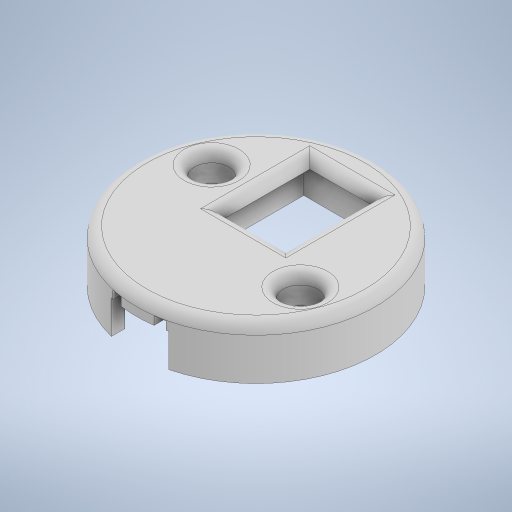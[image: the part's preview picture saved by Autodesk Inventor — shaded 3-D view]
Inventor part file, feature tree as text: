
AUTODESK INVENTOR PART (.ipt)
format: ipt  version: 2023 (Build 270158000, 158)  size: 401,408 bytes
history: native  units: mm
features: extrude x11, sketch x8, fillet x3, plane x2, thread x2, projected_geometry x1
ambient origin geometry x8: Origin, YZ Plane, XZ Plane, XY Plane, X Axis, Y Axis, Z Axis, Center Point
bodies: Solid1 (feature_tree)
feature tree (27):
  sketch  "Sketch1"  dims[d0=30.0mm d1=15.0mm]
  extrude  "Extrusion1"  Depth=30.0mm
  extrude  "Extrusion2"  Depth=16.0mm
  extrude  "Extrusion4"  Depth=8.25mm TaperAngle=0.0deg
  extrude  "Extrusion5"  Depth=8.4mm
  extrude  "Extrusion6"  Depth=1.94mm TaperAngle=0.0deg
  extrude  "Extrusion7"  Depth=1.25mm TaperAngle=0.0deg
  plane  "Work Plane1"
  extrude  "Extrusion9"  Depth=0.3mm
  plane  "Work Plane2"
  fillet  "Fillet3"  Radius=1.5mm
  fillet  "Fillet4"  Radius=1.5mm
  extrude  "Extrusion10"  Depth=1.5mm
  sketch  "Sketch7"  dims[d22=0.3mm d23=0.3mm d24=1.5mm d25=1.5mm]
  extrude  "Extrusion11"  Depth=1.5mm
  extrude  "Extrusion12"  TaperAngle=0.0deg  [1 undecoded]
  fillet  "Fillet5"  [1 undecoded]
  extrude  "Extrusion13"  Depth=1.5mm
  thread  "Thread3"  [1 undecoded]
  thread  "Thread4"  [1 undecoded]
  sketch  "Sketch2"  dims[d2=16.0mm d3=8.0mm]
  sketch  "Sketch3"  dims[d7=1.5mm d8=0.0mm d9=8.25mm d10=0.0mm]
  sketch  "Sketch4"  dims[d11=8.4mm d12=4.2mm]
  sketch  "Sketch5"  dims[d13=35.0mm d16=1.94mm d17=0.0mm]
  sketch  "Sketch6"  dims[d18=1.5mm d19=0.0mm d20=1.25mm d21=0.0mm]
  sketch  "Sketch8"  dims[d26=1.2mm d27=0.0mm d29=12.0mm d32=15.0mm d37=0.0mm d38=0.0mm d39=1.0mm d40=1.0mm d44=5.75mm d45=11.5mm d46=0.0mm d47=0.0mm d48=10.0mm d49=0.0mm d50=0.0mm d51=1.5mm d52=1.5mm d56=0.0mm d57=11.25mm d58=5.625mm d59=24.25mm d60=28.5mm d61=0.0mm d62=0.0mm d63=3.0mm d64=3.0mm d65=11.0mm d66=11.0mm d67=4.5mm d68=4.5mm d69=5.225mm d70=0.0mm d71=5.0mm d72=5.0mm d73=4.125mm d74=0.0mm d75=1.5mm d80=2.0mm d81=0.0mm d82=9.0mm d83=0.0mm d84=9.0mm d85=0.0mm d28=0.5mm d30=0.5mm d31=0.872665mm d43=0.0mm]
  projected_geometry  "Projected Loop1"
note: 4 required parameter values undecoded (feature->parameter linkage not recoverable at this tier; creation-order binding heuristic only, values carry confidence <= 0.55)
